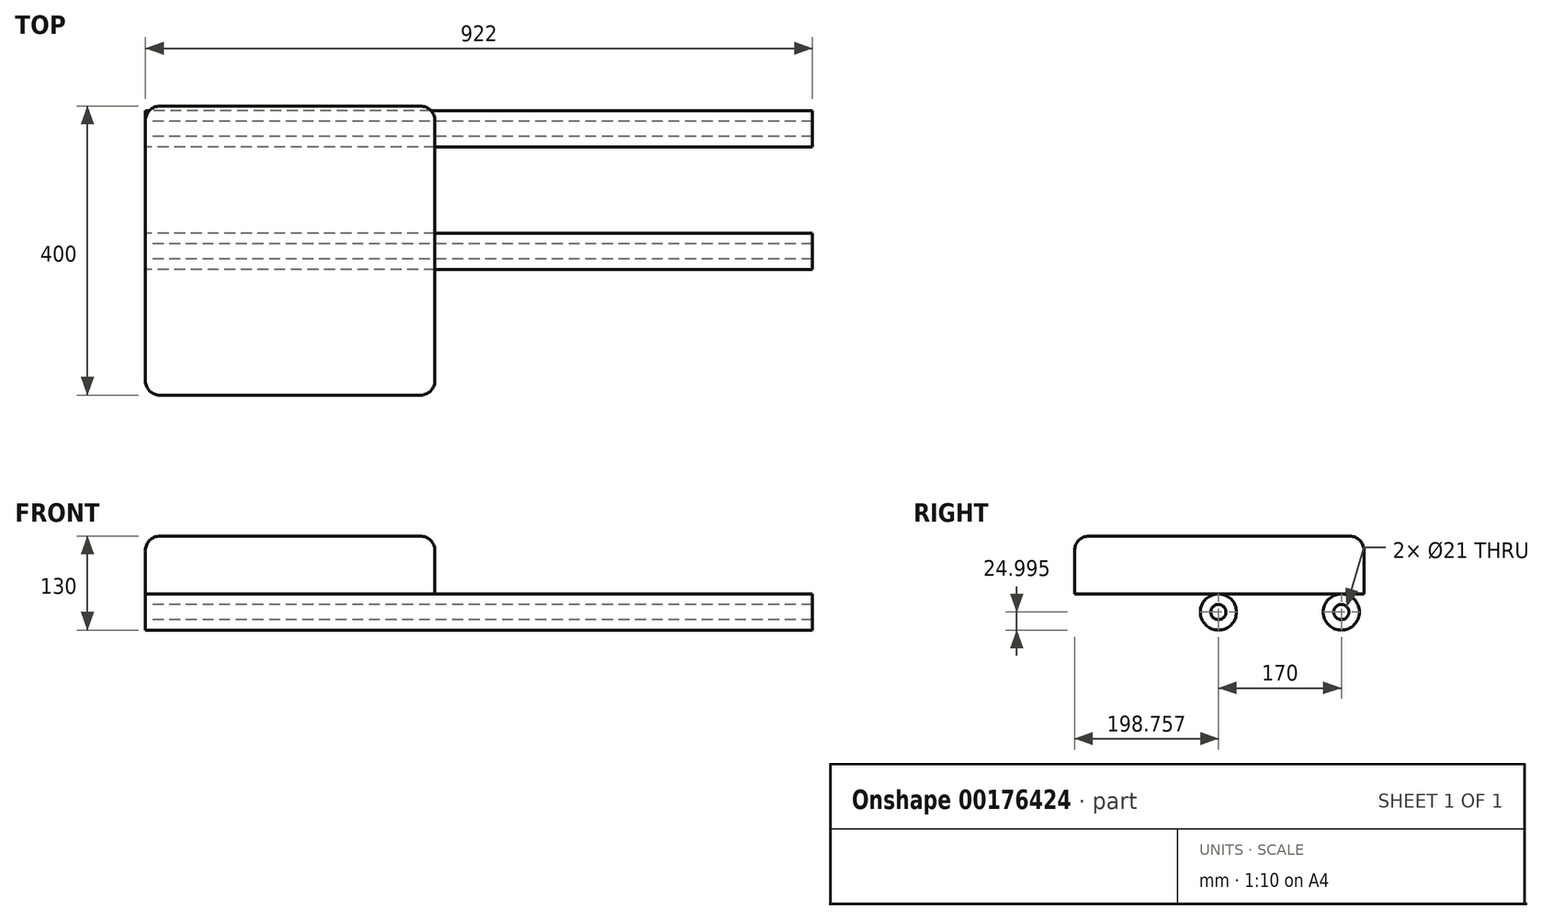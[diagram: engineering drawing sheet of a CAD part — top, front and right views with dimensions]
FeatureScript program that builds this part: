
annotation { "Feature Type Name" : "Feature", "Feature Type Description" : "" }
export const myFeature = defineFeature(function(context is Context, id is Id, definition is map)
    precondition{}
    {
        {
            var Q0;
            Q0=qCreatedBy(makeId("Right.planeOp"),FACE);
            var sketch = newSketch(context, id + "F0", { "sketchPlane" : qUnion([Q0])});
            skPoint(sketch, "E0", {"position": v(109.89, -33.33) * mm});
            skCircle(sketch, "E1", {"center": v(-60.11, -33.33) * mm, "radius": 25 * mm});
            skLineSegment(sketch, "E2", {"start": v(141.13, -8.33) * mm, "end": v(-258.87, -8.33) * mm});
            skLineSegment(sketch, "E3", {"start": v(-258.87, -8.33) * mm, "end": v(-258.87, 71.67) * mm});
            skLineSegment(sketch, "E4", {"start": v(-258.87, 71.67) * mm, "end": v(141.13, 71.67) * mm});
            skLineSegment(sketch, "E5", {"start": v(141.13, 71.67) * mm, "end": v(141.13, -8.33) * mm});
            skLineSegment(sketch, "E6", {"start": v(-60.11, -33.33) * mm, "end": v(165.5, -33.33) * mm});
            skCircle(sketch, "E7", {"center": v(109.89, -33.33) * mm, "radius": 25 * mm});
            skCircle(sketch, "E8", {"center": v(-60.11, -33.33) * mm, "radius": 10.5 * mm});
            skCircle(sketch, "E9", {"center": v(109.89, -33.33) * mm, "radius": 10.5 * mm});
            skSolve(sketch);
        }
        {
            var Q0;
            {var subQ0=sQuery(id+"F0.wireOp",EDGE,"E3");Q0=makeQuery(id+"F0.imprint","IMPRINT",FACE,{"disambiguationData":[TD([[makeQuery(id+"F0.imprint","IMPRINT",EDGE,{"derivedFrom":subQ0}),-1.0]])]});}
            extrude(context, id + "F1", {"entities" : qUnion([Q0]), "depth" : 400 * mm});
        }
        {
            var Q0;
            {var subQ0=sQuery(id+"F0.wireOp",EDGE,"E7");var subQ1=sQuery(id+"F0.wireOp",EDGE,"af3392f4-2e7c-429f-94c4-08223b162b21");var subQ2=makeQuery(id+"F0.imprint","INTERSECT",VERTEX,{"disambiguationData":[OD(0.0)],"derivedFrom":[subQ1,subQ0]});Q0=makeQuery(id+"F0.imprint","IMPRINT",FACE,{"disambiguationData":[TD([[makeQuery(id+"F0.imprint","IMPRINT",EDGE,{"disambiguationData":[TD([[subQ2,1.0]])],"derivedFrom":subQ1}),1.0]])]});}
            var Q1;
            {var subQ0=sQuery(id+"F0.wireOp",EDGE,"E7");var subQ1=sQuery(id+"F0.wireOp",EDGE,"af3392f4-2e7c-429f-94c4-08223b162b21");var subQ2=makeQuery(id+"F0.imprint","INTERSECT",VERTEX,{"disambiguationData":[OD(0.0)],"derivedFrom":[subQ1,subQ0]});Q1=makeQuery(id+"F0.imprint","IMPRINT",FACE,{"disambiguationData":[TD([[makeQuery(id+"F0.imprint","IMPRINT",EDGE,{"disambiguationData":[TD([[subQ2,1.0]])],"derivedFrom":subQ1}),-1.0]])]});}
            var Q2;
            {var subQ0=sQuery(id+"F0.wireOp",EDGE,"E7");var subQ1=sQuery(id+"F0.wireOp",EDGE,"E6");var subQ2=makeQuery(id+"F0.imprint","INTERSECT",VERTEX,{"disambiguationData":[OD(0.0)],"derivedFrom":[subQ1,subQ0]});Q2=makeQuery(id+"F0.imprint","IMPRINT",FACE,{"disambiguationData":[TD([[makeQuery(id+"F0.imprint","IMPRINT",EDGE,{"disambiguationData":[TD([[subQ2,1.0]])],"derivedFrom":subQ1}),1.0]])]});}
            var Q3;
            {var subQ0=sQuery(id+"F0.wireOp",EDGE,"af3392f4-2e7c-429f-94c4-08223b162b21");var subQ1=sQuery(id+"F0.wireOp",EDGE,"E1");var subQ2=makeQuery(id+"F0.imprint","INTERSECT",VERTEX,{"derivedFrom":[subQ1,subQ0]});Q3=makeQuery(id+"F0.imprint","IMPRINT",FACE,{"disambiguationData":[TD([[makeQuery(id+"F0.imprint","IMPRINT",EDGE,{"disambiguationData":[TD([[subQ2,-1.0]])],"derivedFrom":subQ1}),1.0]])]});}
            var Q4;
            {var subQ0=sQuery(id+"F0.wireOp",EDGE,"af3392f4-2e7c-429f-94c4-08223b162b21");var subQ1=sQuery(id+"F0.wireOp",EDGE,"E1");var subQ2=makeQuery(id+"F0.imprint","INTERSECT",VERTEX,{"derivedFrom":[subQ1,subQ0]});Q4=makeQuery(id+"F0.imprint","IMPRINT",FACE,{"disambiguationData":[TD([[makeQuery(id+"F0.imprint","IMPRINT",EDGE,{"disambiguationData":[TD([[subQ2,1.0]])],"derivedFrom":subQ1}),1.0]])]});}
            var Q5;
            {var subQ0=sQuery(id+"F0.wireOp",EDGE,"E7");var subQ1=sQuery(id+"F0.wireOp",EDGE,"E6");var subQ2=makeQuery(id+"F0.imprint","INTERSECT",VERTEX,{"disambiguationData":[OD(1.0)],"derivedFrom":[subQ1,subQ0]});Q5=makeQuery(id+"F0.imprint","IMPRINT",FACE,{"disambiguationData":[TD([[makeQuery(id+"F0.imprint","IMPRINT",EDGE,{"disambiguationData":[TD([[subQ2,-1.0]])],"derivedFrom":subQ1}),-1.0]])]});}
            extrude(context, id + "F2", {"entities" : qUnion([Q0, Q1, Q2, Q3, Q4, Q5]), "operationType" : NewBodyOperationType.ADD, "depth" : 922 * mm});
        }
        {
            var Q0;
            Q0=makeQuery(id+"F1.opExtrude","SWEPT_EDGE",EDGE,{"disambiguationData":[OSD([sQuery(id+"F0.wireOp",EDGE,"E3"),sQuery(id+"F0.wireOp",EDGE,"E4")])]});
            var Q1;
            Q1=makeQuery(id+"F1.opExtrude","CAP_EDGE",EDGE,{"disambiguationData":[OSD([sQuery(id+"F0.wireOp",EDGE,"E4")])],"isStart":false});
            var Q2;
            Q2=makeQuery(id+"F1.opExtrude","SWEPT_EDGE",EDGE,{"disambiguationData":[OSD([sQuery(id+"F0.wireOp",EDGE,"E4"),sQuery(id+"F0.wireOp",EDGE,"E5")])]});
            var Q3;
            Q3=makeQuery(id+"F1.opExtrude","CAP_EDGE",EDGE,{"disambiguationData":[OSD([sQuery(id+"F0.wireOp",EDGE,"E4")])],"isStart":true});
            var Q4;
            Q4=makeQuery(id+"F1.opExtrude","CAP_EDGE",EDGE,{"disambiguationData":[OSD([sQuery(id+"F0.wireOp",EDGE,"E5")])],"isStart":false});
            var Q5;
            Q5=makeQuery(id+"F1.opExtrude","CAP_EDGE",EDGE,{"disambiguationData":[OSD([sQuery(id+"F0.wireOp",EDGE,"E5")])],"isStart":true});
            var Q6;
            Q6=makeQuery(id+"F1.opExtrude","CAP_EDGE",EDGE,{"disambiguationData":[OSD([sQuery(id+"F0.wireOp",EDGE,"E3")])],"isStart":false});
            var Q7;
            Q7=makeQuery(id+"F1.opExtrude","CAP_EDGE",EDGE,{"disambiguationData":[OSD([sQuery(id+"F0.wireOp",EDGE,"E3")])],"isStart":true});
            fillet(context, id + "F3", {"entities" : qUnion([Q0, Q1, Q2, Q3, Q4, Q5, Q6, Q7]), "radius" : 20 * mm, "tangentPropagation" : true, "allowEdgeOverflow" : false});
        }
    });
